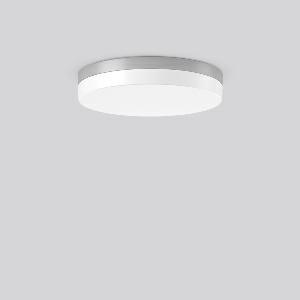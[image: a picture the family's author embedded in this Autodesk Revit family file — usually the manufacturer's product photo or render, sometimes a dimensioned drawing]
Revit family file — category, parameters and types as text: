
# Revit family: flat_slim_round_312631_004_1b94
name_source: partatom
category: Lighting Fixtures
units: mm (PartAtom-declared; Revit-internal decimal feet)

## family parameters
Cut with Voids When Loaded = No
Host = Face
Light Source = No
Part Type = Normal
Room Calculation Point = No
Round Connector Dimension = Use Diameter
Shared = No

## types (1)
- MultiLumen 1 830 (1 x LED Modul 830, 2450 lm, 3000)
    Apparent Load = 25 VA
    CIE Flux Codes = 40 70 90 84 100
    Color Rendering = 80
    Color Temperature = 3000
    Default Elevation = 1800 mm
    Height = 75 mm
    Lamp = 1 x LED Modul 830
    Lamp Light Flux = 2450 lm
    Lamp count = 1
    Length = 400 mm
    Lifetime = 50000 h
    Luminous efficacy = 98 lm/W
    Manufacturer = RZB
    ModVariant = No
    Model = 312631.004
    Mounting Place = Ceiling
    Mounting Type = Surface mounted
    Number of Poles = 1
    OnlyDefault = Yes
    Power Factor = 1
    Product Name = FLAT SLIM round
    Product group = Surface mounted ceiling and wall luminaires
    ProductGroupID = 305
    Protection Class = Protection class I
    Protection Degree = Degree of protection
    RLX_Detail_Level = 1
    RLX_Emergency_Light_Flux = 0 lm
    RLX_Emergency_Type = 0
    RLX_Emergency_Type_DB = No
    RlxData = <blob elided: 20305 chars, md5=359b4687>
    Socket = socket
    Standby Power = 0 W
    System Light Flux = 2450 lm
    System Power = 25 W
    Type Comments = MultiLumen 1 830
    Type Image = 312631.004.jpg
    URL = http://relux.com
    VarID = multilumen_1_830
    Voltage = 0 V
    Weight = 0.00 kg
    Width = 0 mm  [stored 0 ft]

note: [stored X ft] marks values corroborated as IEEE doubles in the binary element streams (Revit-internal decimal feet)

## geometry (parser evidence)
native form markers: Blend x4, Sweep x14
no freeform markers — native parametric forms only
